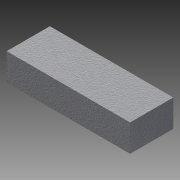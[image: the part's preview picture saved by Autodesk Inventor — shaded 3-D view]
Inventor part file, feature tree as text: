
AUTODESK INVENTOR PART (.ipt)
format: ipt  version: 2015 (Build 190159000, 159)  size: 102,400 bytes
history: native  units: mm
features: other x1, extrude x1, sketch x1
ambient origin geometry x8: Origin, YZ Plane, XZ Plane, XY Plane, X Axis, Y Axis, Z Axis, Center Point
bodies: Body1 (feature_tree)
feature tree (3):
  other  "ソリッド1"
  extrude  "押し出し1"  Depth=100.0mm
  sketch  "スケッチ1"
